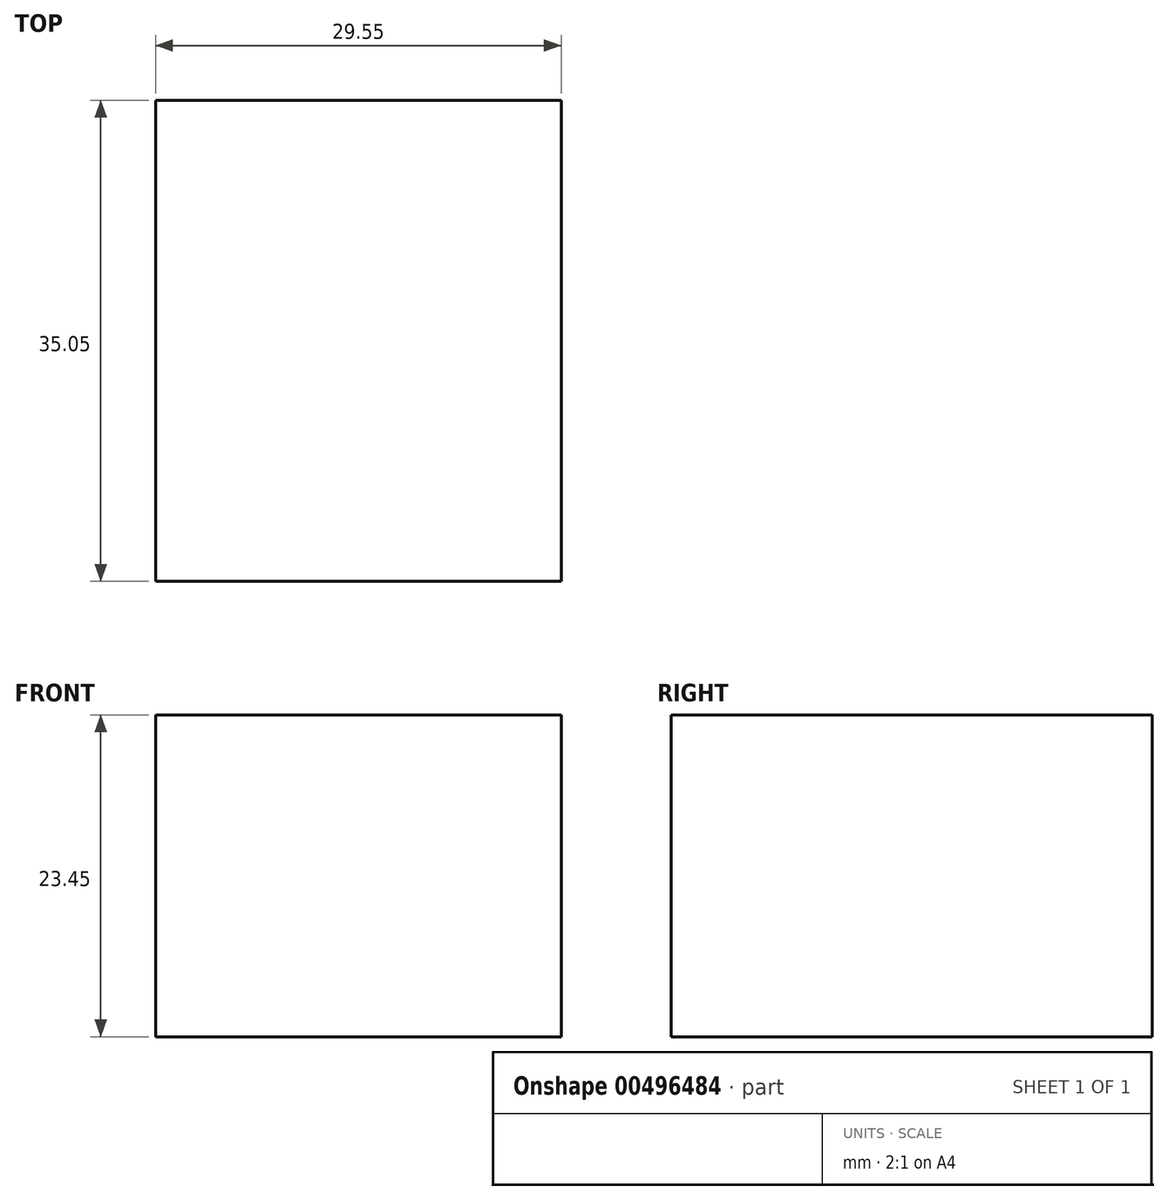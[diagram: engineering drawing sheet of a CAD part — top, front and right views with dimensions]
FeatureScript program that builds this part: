
annotation { "Feature Type Name" : "Feature", "Feature Type Description" : "" }
export const myFeature = defineFeature(function(context is Context, id is Id, definition is map)
    precondition{}
    {
        {
            var Q0;
            Q0=qCreatedBy(makeId("Top.planeOp"),FACE);
            var sketch = newSketch(context, id + "F0", { "sketchPlane" : qUnion([Q0])});
            skLineSegment(sketch, "E0.bottom", {"start": v(-29.55, 35.05) * mm, "end": v(0, 35.05) * mm});
            skLineSegment(sketch, "E0.top", {"start": v(-29.55, 0) * mm, "end": v(0, 0) * mm});
            skLineSegment(sketch, "E0.left", {"start": v(-29.55, 35.05) * mm, "end": v(-29.55, 0) * mm});
            skLineSegment(sketch, "E0.right", {"start": v(0, 35.05) * mm, "end": v(0, 0) * mm});
            skSolve(sketch);
        }
        {
            var Q0;
            Q0=makeQuery(id+"F0.imprint","IMPRINT",FACE,{"disambiguationData":[TD([[makeQuery(id+"F0.imprint","IMPRINT",EDGE,{"derivedFrom":sQuery(id+"F0.wireOp",EDGE,"E0.bottom")}),-1.0]])]});
            extrude(context, id + "F1", {"entities" : qUnion([Q0]), "depth" : 23.45 * mm});
        }
    });
